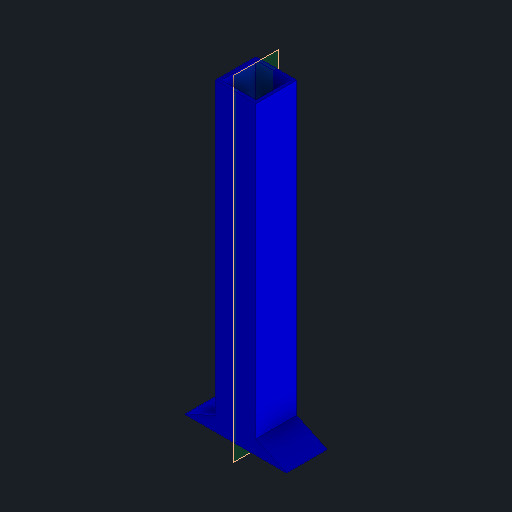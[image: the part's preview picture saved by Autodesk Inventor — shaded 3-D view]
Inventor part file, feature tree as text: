
AUTODESK INVENTOR PART (.ipt)
format: ipt  version: 2024 (Build 280153000, 153)  size: 156,160 bytes
history: native  units: mm
features: other x2, extrude x2, sketch x2, mirror x1
ambient origin geometry x8: Origin, YZ Plane, XZ Plane, XY Plane, X Axis, Y Axis, Z Axis, Center Point
bodies: Body1 (feature_tree)
feature tree (7):
  other  "Твердое тело1"
  extrude  "Выдавливание1"  Depth=20.0mm
  extrude  "Выдавливание2"  Depth=1.5mm
  other  "РабПлоскость1"
  mirror  "Зеркальное отражение1"
  sketch  "Эскиз1"
  sketch  "Эскиз3"
